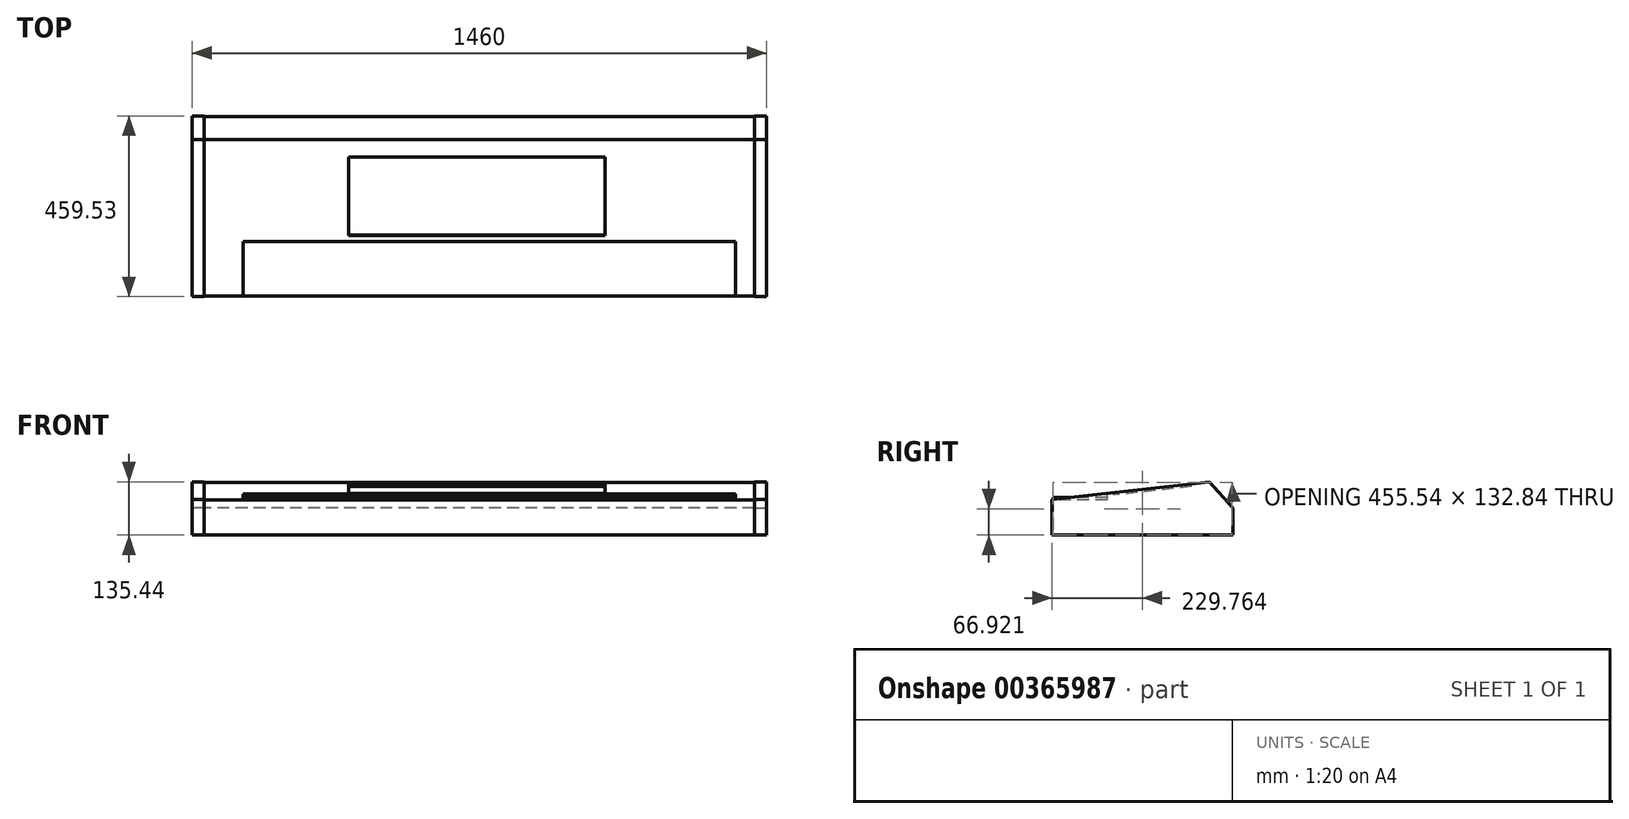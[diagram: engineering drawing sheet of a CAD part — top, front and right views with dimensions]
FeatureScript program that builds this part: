
annotation { "Feature Type Name" : "Feature", "Feature Type Description" : "" }
export const myFeature = defineFeature(function(context is Context, id is Id, definition is map)
    precondition{}
    {
        {
            var Q0;
            Q0=qCreatedBy(makeId("Right.planeOp"),FACE);
            var sketch = newSketch(context, id + "F0", { "sketchPlane" : qUnion([Q0])});
            skPoint(sketch, "E0", {"position": v(-300.15, -49.72) * mm});
            skPoint(sketch, "E1", {"position": v(99.85, -5.28) * mm});
            skLineSegment(sketch, "E2", {"start": v(159.38, -71.43) * mm, "end": v(99.85, -5.28) * mm});
            skLineSegment(sketch, "E3", {"start": v(-300.15, -49.72) * mm, "end": v(99.85, -5.28) * mm});
            skLineSegment(sketch, "E4", {"start": v(-300.15, -49.72) * mm, "end": v(-300.15, -140.72) * mm});
            skLineSegment(sketch, "E5", {"start": v(159.38, -71.43) * mm, "end": v(159.38, -140.72) * mm});
            skLineSegment(sketch, "E6", {"start": v(159.38, -140.72) * mm, "end": v(-300.15, -140.72) * mm});
            skLineSegment(sketch, "E7", {"start": v(-298.15, -51.51) * mm, "end": v(99.05, -7.38) * mm});
            skLineSegment(sketch, "E8", {"start": v(-298.15, -51.51) * mm, "end": v(-298.15, -140.22) * mm});
            skLineSegment(sketch, "E9", {"start": v(99.05, -7.38) * mm, "end": v(157.38, -72.2) * mm});
            skLineSegment(sketch, "E10", {"start": v(157.38, -72.2) * mm, "end": v(157.38, -140.22) * mm});
            skLineSegment(sketch, "E11", {"start": v(157.38, -140.22) * mm, "end": v(-298.15, -140.22) * mm});
            skSolve(sketch);
        }
        {
            var Q0;
            Q0=makeQuery(id+"F0.imprint","IMPRINT",FACE,{"disambiguationData":[TD([[makeQuery(id+"F0.imprint","IMPRINT",EDGE,{"derivedFrom":sQuery(id+"F0.wireOp",EDGE,"E7")}),-1.0]])]});
            extrude(context, id + "F1", {"entities" : qUnion([Q0]), "depth" : 1460 * mm});
        }
        {
            var Q0;
            Q0=makeQuery(id+"F0.imprint","IMPRINT",FACE,{"disambiguationData":[TD([[makeQuery(id+"F0.imprint","IMPRINT",EDGE,{"derivedFrom":sQuery(id+"F0.wireOp",EDGE,"E2")}),1.0]])]});
            extrude(context, id + "F2", {"entities" : qUnion([Q0]), "operationType" : NewBodyOperationType.ADD, "depth" : 31 * mm});
        }
        {
            var Q0;
            Q0=makeQuery(id+"F1.opExtrude","CAP_FACE",FACE,{"disambiguationData":[OSD([sQuery(id+"F0.wireOp",EDGE,"E7"),sQuery(id+"F0.wireOp",EDGE,"E8"),sQuery(id+"F0.wireOp",EDGE,"E9"),sQuery(id+"F0.wireOp",EDGE,"E10"),sQuery(id+"F0.wireOp",EDGE,"E11")])],"isStart":false});
            var sketch = newSketch(context, id + "F3", { "sketchPlane" : qUnion([Q0])});
            skPoint(sketch, "E12", {"position": v(-300.15, -49.72) * mm});
            skPoint(sketch, "E13", {"position": v(99.85, -5.28) * mm});
            skLineSegment(sketch, "E14", {"start": v(159.38, -71.43) * mm, "end": v(99.85, -5.28) * mm});
            skLineSegment(sketch, "E15", {"start": v(-300.15, -49.72) * mm, "end": v(99.85, -5.28) * mm});
            skLineSegment(sketch, "E16", {"start": v(-300.15, -49.72) * mm, "end": v(-300.15, -140.72) * mm});
            skLineSegment(sketch, "E17", {"start": v(159.38, -71.43) * mm, "end": v(159.38, -140.72) * mm});
            skLineSegment(sketch, "E18", {"start": v(159.38, -140.72) * mm, "end": v(-300.15, -140.72) * mm});
            skLineSegment(sketch, "E19", {"start": v(-298.15, -51.51) * mm, "end": v(99.05, -7.38) * mm});
            skLineSegment(sketch, "E20", {"start": v(-298.15, -51.51) * mm, "end": v(-298.15, -140.22) * mm});
            skLineSegment(sketch, "E21", {"start": v(99.05, -7.38) * mm, "end": v(157.38, -72.2) * mm});
            skLineSegment(sketch, "E22", {"start": v(157.38, -72.2) * mm, "end": v(157.38, -140.22) * mm});
            skLineSegment(sketch, "E23", {"start": v(157.38, -140.22) * mm, "end": v(-298.15, -140.22) * mm});
            skSolve(sketch);
        }
        {
            var Q0;
            Q0=makeQuery(id+"F3.imprint","IMPRINT",FACE,{"disambiguationData":[TD([[makeQuery(id+"F3.imprint","IMPRINT",EDGE,{"derivedFrom":sQuery(id+"F3.wireOp",EDGE,"E14")}),1.0]])]});
            extrude(context, id + "F4", {"entities" : qUnion([Q0]), "operationType" : NewBodyOperationType.ADD, "oppositeDirection" : true, "depth" : 31 * mm});
        }
        {
            var Q0;
            Q0=makeQuery(id+"F1.opExtrude","SWEPT_FACE",FACE,{"disambiguationData":[OSD([sQuery(id+"F0.wireOp",EDGE,"E7")])]});
            var sketch = newSketch(context, id + "F5", { "sketchPlane" : qUnion([Q0])});
            skLineSegment(sketch, "E24.bottom", {"start": v(398, 52.63) * mm, "end": v(1049, 52.63) * mm});
            skLineSegment(sketch, "E24.top", {"start": v(398, -147.37) * mm, "end": v(1049, -147.37) * mm});
            skLineSegment(sketch, "E24.left", {"start": v(398, 52.63) * mm, "end": v(398, -147.37) * mm});
            skLineSegment(sketch, "E24.right", {"start": v(1049, 52.63) * mm, "end": v(1049, -147.37) * mm});
            skSolve(sketch);
        }
        {
            var Q0;
            Q0=makeQuery(id+"F5.imprint","IMPRINT",FACE,{"disambiguationData":[TD([[makeQuery(id+"F5.imprint","IMPRINT",EDGE,{"derivedFrom":sQuery(id+"F5.wireOp",EDGE,"E24.bottom")}),-1.0]])]});
            extrude(context, id + "F6", {"entities" : qUnion([Q0]), "operationType" : NewBodyOperationType.REMOVE, "oppositeDirection" : true, "depth" : 5 * mm});
        }
        {
            var Q0;
            Q0=makeQuery(id+"F1.opExtrude","SWEPT_FACE",FACE,{"disambiguationData":[OSD([sQuery(id+"F0.wireOp",EDGE,"E8")])]});
            var sketch = newSketch(context, id + "F7", { "sketchPlane" : qUnion([Q0])});
            skLineSegment(sketch, "E25.bottom", {"start": v(130.28, -16.67) * mm, "end": v(1381.56, -16.67) * mm});
            skLineSegment(sketch, "E25.top", {"start": v(130.28, -72.16) * mm, "end": v(1381.56, -72.16) * mm});
            skLineSegment(sketch, "E25.left", {"start": v(130.28, -16.67) * mm, "end": v(130.28, -72.16) * mm});
            skLineSegment(sketch, "E25.right", {"start": v(1381.56, -16.67) * mm, "end": v(1381.56, -72.16) * mm});
            skLineSegment(sketch, "E26.bottom", {"start": v(1381.56, -72.16) * mm, "end": v(130.28, -72.16) * mm});
            skLineSegment(sketch, "E26.top", {"start": v(1381.56, -33.93) * mm, "end": v(130.28, -33.93) * mm});
            skLineSegment(sketch, "E26.left", {"start": v(1381.56, -72.16) * mm, "end": v(1381.56, -33.93) * mm});
            skLineSegment(sketch, "E26.right", {"start": v(130.28, -72.16) * mm, "end": v(130.28, -33.93) * mm});
            skLineSegment(sketch, "E27", {"start": v(130.28, -44.71) * mm, "end": v(1381.56, -44.71) * mm});
            skSolve(sketch);
        }
        {
            var Q0;
            {var subQ0=sQuery(id+"F7.wireOp",EDGE,"E26.bottom");Q0=makeQuery(id+"F7.imprint","IMPRINT",FACE,{"disambiguationData":[TD([[makeQuery(id+"F7.imprint","IMPRINT",EDGE,{"derivedFrom":subQ0}),-1.0]])]});}
            var Q1;
            {var subQ0=sQuery(id+"F7.wireOp",EDGE,"E26.top");Q1=makeQuery(id+"F7.imprint","IMPRINT",FACE,{"disambiguationData":[TD([[makeQuery(id+"F7.imprint","IMPRINT",EDGE,{"derivedFrom":subQ0}),1.0]])]});}
            var Q2;
            {var subQ0=sQuery(id+"F7.wireOp",EDGE,"E27");Q2=makeQuery(id+"F7.imprint","IMPRINT",FACE,{"disambiguationData":[TD([[makeQuery(id+"F7.imprint","IMPRINT",EDGE,{"derivedFrom":subQ0}),-1.0]])]});}
            extrude(context, id + "F8", {"entities" : qUnion([Q0, Q1, Q2]), "operationType" : NewBodyOperationType.REMOVE, "oppositeDirection" : true, "depth" : 138 * mm});
        }
        {
            var Q0;
            {var subQ0=sQuery(id+"F7.wireOp",EDGE,"E26.bottom");Q0=makeQuery(id+"F7.imprint","IMPRINT",FACE,{"disambiguationData":[TD([[makeQuery(id+"F7.imprint","IMPRINT",EDGE,{"derivedFrom":subQ0}),-1.0]])]});}
            var Q1;
            {var subQ0=sQuery(id+"F7.wireOp",EDGE,"E27");Q1=makeQuery(id+"F7.imprint","IMPRINT",FACE,{"disambiguationData":[TD([[makeQuery(id+"F7.imprint","IMPRINT",EDGE,{"derivedFrom":subQ0}),-1.0]])]});}
            extrude(context, id + "F9", {"entities" : qUnion([Q0, Q1]), "oppositeDirection" : true, "depth" : 138 * mm});
        }
    });
